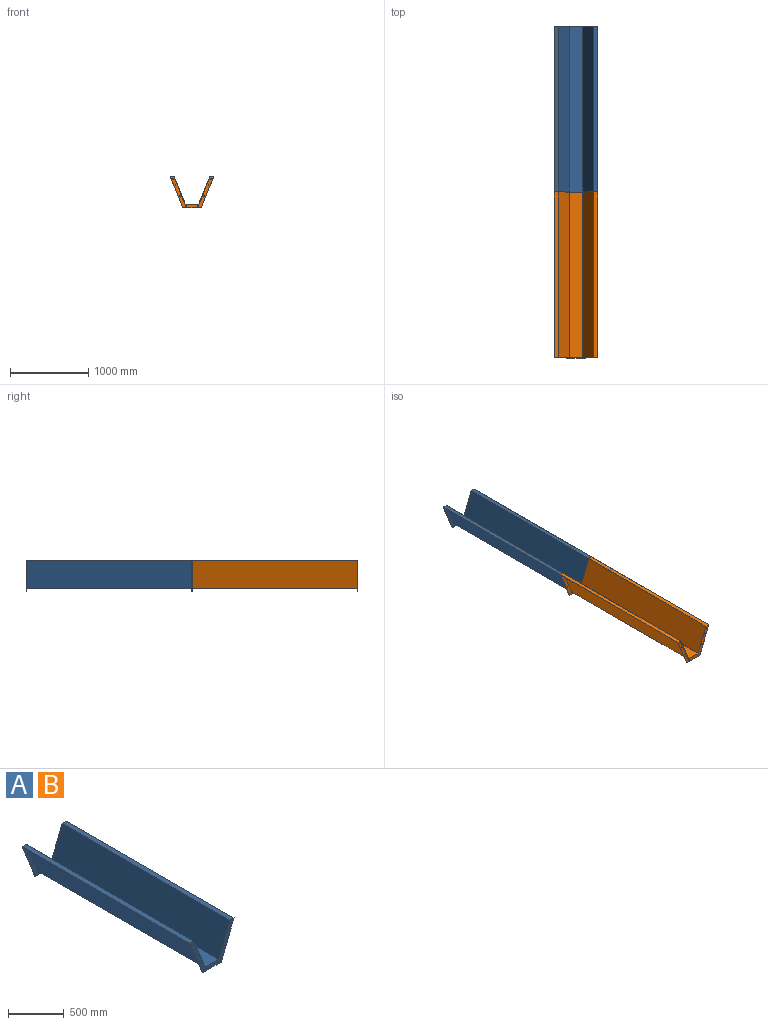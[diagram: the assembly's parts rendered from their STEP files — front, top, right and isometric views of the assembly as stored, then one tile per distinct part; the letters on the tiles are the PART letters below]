
ASSEMBLY  parts=2 mates=1
PART A: 34 faces, bbox 559.8x2123.5x403.2 mm
  f0: plane 2123.47x403.2mm, normal (-0.93,0,-0.37), area 14986.6mm2, adj f1,f2,f4,f7,f10,f11,f14,f17
  f1: plane 236.12x4.76mm, normal (0,0,-1), area 1124.5mm2, adj f0,f3,f4,f11
  f2: plane 236.12x4.76mm, normal (0,0,-1), area 1124.5mm2, adj f0,f3,f10,f17
  f3: plane 2123.47x403.2mm, normal (0.93,0,-0.37), area 14986.6mm2, adj f1,f2,f4,f6,f10,f11,f13,f17
  f4: plane 559.78x403.2mm, normal (0,-1,0), area 47989.4mm2, adj f0,f1,f3,f5,f6,f7,f8,f9
  f5: plane 2123.47x355.6mm, normal (-0.93,0,0.37), area 813658.4mm2, adj f4,f6,f9,f10
  f6: plane 2123.47x51.29mm, normal (0,0,1), area 108917.9mm2, adj f3,f4,f5,f10
  f7: plane 2123.47x51.29mm, normal (0,0,1), area 108917.9mm2, adj f0,f4,f8,f10
  f8: plane 2123.47x355.6mm, normal (0.93,0,0.37), area 813658.4mm2, adj f4,f7,f9,f10
  f9: plane 2123.47x171.75mm, normal (0,0,1), area 364703mm2, adj f4,f5,f8,f10
  f10: plane 559.78x403.2mm, normal (0,1,0), area 47989.4mm2, adj f0,f2,f3,f5,f6,f7,f8,f9
  f11: plane 555.96x398.44mm, normal (0,1,0), area 43042.3mm2, adj f0,f1,f3,f12,f13,f14,f15,f16
  f12: plane 2113.95x355.6mm, normal (0.93,0,-0.37), area 810008.7mm2, adj f11,f13,f16,f17
  f13: plane 2113.95x46.16mm, normal (0,0,-1), area 97581.1mm2, adj f3,f11,f12,f17
  f14: plane 2113.95x46.16mm, normal (0,0,-1), area 97581.1mm2, adj f0,f11,f15,f17
  f15: plane 2113.95x355.6mm, normal (-0.93,0,-0.37), area 810008.7mm2, adj f11,f14,f16,f17
  f16: plane 2113.95x178.19mm, normal (0,0,-1), area 376682.1mm2, adj f11,f12,f15,f17
  f17: plane 555.96x398.44mm, normal (0,-1,0), area 43042.3mm2, adj f0,f2,f3,f12,f13,f14,f15,f16
  f18: cylinder r=5.04mm len=10.08mm, axis (0,-1,0), area 150.9mm2, adj f10,f17
  f19: cylinder r=5.04mm len=10.08mm, axis (0,-1,0), area 150.9mm2, adj f10,f17
  f20: cylinder r=5.04mm len=10.08mm, axis (0,-1,0), area 150.9mm2, adj f10,f17
  f21: cylinder r=5.04mm len=10.08mm, axis (0,-1,0), area 150.9mm2, adj f10,f17
  f22: cylinder r=5.04mm len=10.08mm, axis (0,-1,0), area 150.9mm2, adj f10,f17
  f23: cylinder r=5.04mm len=10.08mm, axis (0,-1,0), area 150.9mm2, adj f10,f17
  f24: cylinder r=5.04mm len=10.08mm, axis (0,-1,0), area 150.9mm2, adj f10,f17
  f25: cylinder r=5.04mm len=10.08mm, axis (0,-1,0), area 150.9mm2, adj f10,f17
  f26: cylinder r=5.04mm len=10.08mm, axis (0,-1,0), area 150.9mm2, adj f4,f11
  f27: cylinder r=5.04mm len=10.08mm, axis (0,-1,0), area 150.9mm2, adj f4,f11
  f28: cylinder r=5.04mm len=10.08mm, axis (0,-1,0), area 150.9mm2, adj f4,f11
  f29: cylinder r=5.04mm len=10.08mm, axis (0,-1,0), area 150.9mm2, adj f4,f11
  f30: cylinder r=5.04mm len=10.08mm, axis (0,-1,0), area 150.9mm2, adj f4,f11
  f31: cylinder r=5.04mm len=10.08mm, axis (0,-1,0), area 150.9mm2, adj f4,f11
  f32: cylinder r=5.04mm len=10.08mm, axis (0,-1,0), area 150.9mm2, adj f4,f11
  f33: cylinder r=5.04mm len=10.08mm, axis (0,-1,0), area 150.9mm2, adj f4,f11
PART B: same geometry as A
PLACE A t=(1354.26,5170.4,6749.09)mm
PLACE B t=(1354.26,3046.92,6749.09)mm fixed
MATE fastened A.f6 <-> B.f6  axis (0,0,1) through (91.53,3049.59,831.83)mm
